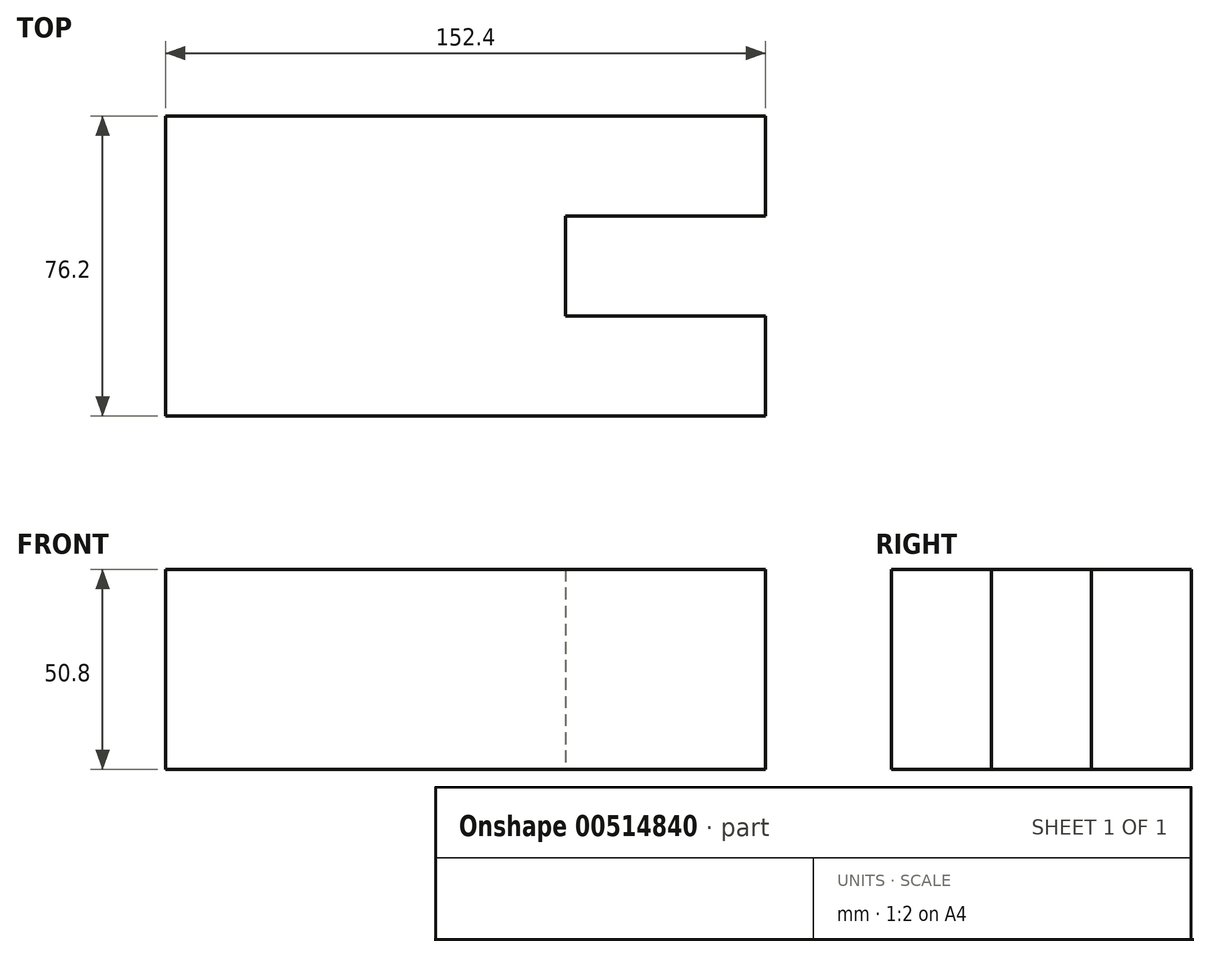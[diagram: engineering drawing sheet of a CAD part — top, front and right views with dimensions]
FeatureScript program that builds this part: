
annotation { "Feature Type Name" : "Feature", "Feature Type Description" : "" }
export const myFeature = defineFeature(function(context is Context, id is Id, definition is map)
    precondition{}
    {
        {
            var Q0;
            Q0=qCreatedBy(makeId("Top.planeOp"),FACE);
            var sketch = newSketch(context, id + "F0", { "sketchPlane" : qUnion([Q0])});
            skLineSegment(sketch, "E0", {"start": v(-69.75, 42.57) * mm, "end": v(-69.75, -33.63) * mm});
            skLineSegment(sketch, "E1", {"start": v(-69.75, -33.63) * mm, "end": v(82.65, -33.63) * mm});
            skLineSegment(sketch, "E2", {"start": v(82.65, -33.63) * mm, "end": v(82.65, -8.23) * mm});
            skLineSegment(sketch, "E3", {"start": v(82.65, -8.23) * mm, "end": v(31.85, -8.23) * mm});
            skLineSegment(sketch, "E4", {"start": v(31.85, -8.23) * mm, "end": v(31.85, 17.17) * mm});
            skLineSegment(sketch, "E5", {"start": v(31.85, 17.17) * mm, "end": v(82.65, 17.17) * mm});
            skLineSegment(sketch, "E6", {"start": v(82.65, 17.17) * mm, "end": v(82.65, 42.57) * mm});
            skLineSegment(sketch, "E7", {"start": v(82.65, 42.57) * mm, "end": v(-69.75, 42.57) * mm});
            skSolve(sketch);
        }
        {
            var Q0;
            Q0=makeQuery(id+"F0.imprint","IMPRINT",FACE,{"disambiguationData":[TD([[makeQuery(id+"F0.imprint","IMPRINT",EDGE,{"derivedFrom":sQuery(id+"F0.wireOp",EDGE,"E0")}),1.0]])]});
            extrude(context, id + "F1", {"entities" : qUnion([Q0]), "depth" : 50.8 * mm, "offsetDistance" : 25.4 * mm});
        }
    });
